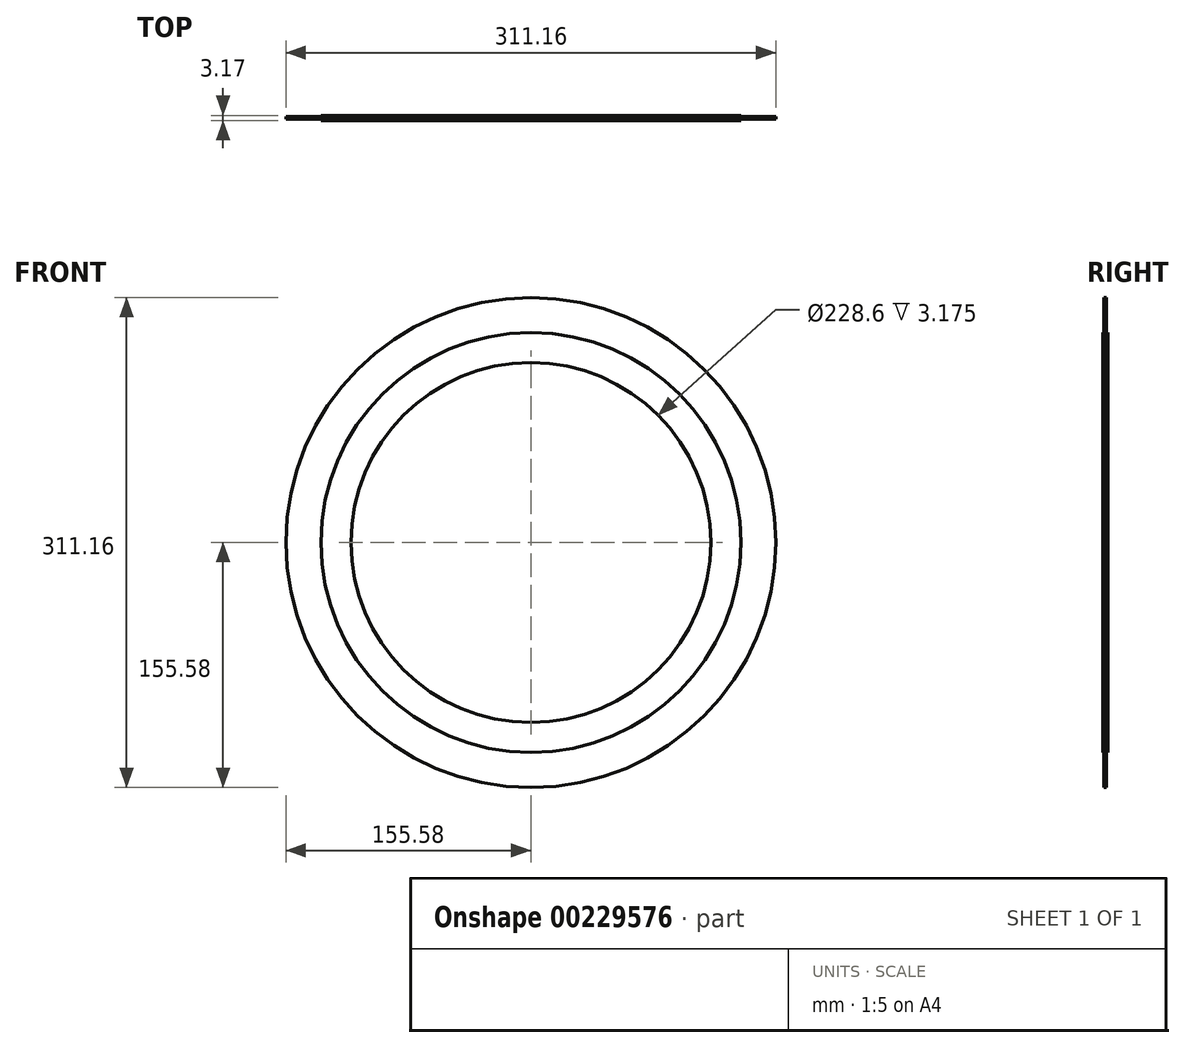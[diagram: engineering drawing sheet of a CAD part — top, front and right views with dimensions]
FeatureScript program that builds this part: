
annotation { "Feature Type Name" : "Feature", "Feature Type Description" : "" }
export const myFeature = defineFeature(function(context is Context, id is Id, definition is map)
    precondition{}
    {
        {
            var Q0;
            Q0=qCreatedBy(makeId("Front.planeOp"),FACE);
            var sketch = newSketch(context, id + "F0", { "sketchPlane" : qUnion([Q0])});
            skCircle(sketch, "E0", {"center": v(0, 0) * mm, "radius": 114.3 * mm});
            skCircle(sketch, "E1", {"center": v(0, 0) * mm, "radius": 155.58 * mm});
            skSolve(sketch);
        }
        {
            var Q0;
            Q0 = qSketchRegion(id + "F0", true);
            extrude(context, id + "F1", {"entities" : qUnion([Q0]), "depth" : 1.59 * mm});
        }
        {
            var Q0;
            Q0=qCreatedBy(makeId("Front.planeOp"),FACE);
            cPlane(context, id + "F2", {"entities" : qUnion([Q0]), "cplaneType" : CPlaneType.OFFSET, "offset" : 1.59 * mm, "width" : 152.4 * mm, "height" : 152.4 * mm});
        }
        {
            var Q0;
            Q0=qCreatedBy(makeId("Front.planeOp"),FACE);
            cPlane(context, id + "F3", {"entities" : qUnion([Q0]), "cplaneType" : CPlaneType.OFFSET, "offset" : 0.8 * mm, "width" : 152.4 * mm, "height" : 152.4 * mm});
        }
        {
            var Q0;
            Q0=qCreatedBy(id+"F3.planeOp",FACE);
            var sketch = newSketch(context, id + "F4", { "sketchPlane" : qUnion([Q0])});
            skCircle(sketch, "E2", {"center": v(0, 0) * mm, "radius": 114.3 * mm});
            skCircle(sketch, "E3", {"center": v(0, 0) * mm, "radius": 133.35 * mm});
            skSolve(sketch);
        }
        {
            var Q0;
            Q0 = qSketchRegion(id + "F4", true);
            extrude(context, id + "F5", {"entities" : qUnion([Q0]), "operationType" : NewBodyOperationType.ADD, "oppositeDirection" : true, "depth" : 1.59 * mm});
        }
        {
            var Q0;
            Q0=qCreatedBy(id+"F2.planeOp",FACE);
            var sketch = newSketch(context, id + "F6", { "sketchPlane" : qUnion([Q0])});
            skCircle(sketch, "E4", {"center": v(0, 0) * mm, "radius": 114.3 * mm});
            skCircle(sketch, "E5", {"center": v(0, 0) * mm, "radius": 133.35 * mm});
            skSolve(sketch);
        }
        {
            var Q0;
            Q0 = qSketchRegion(id + "F6", true);
            extrude(context, id + "F7", {"entities" : qUnion([Q0]), "operationType" : NewBodyOperationType.ADD, "depth" : 0.8 * mm});
        }
    });
